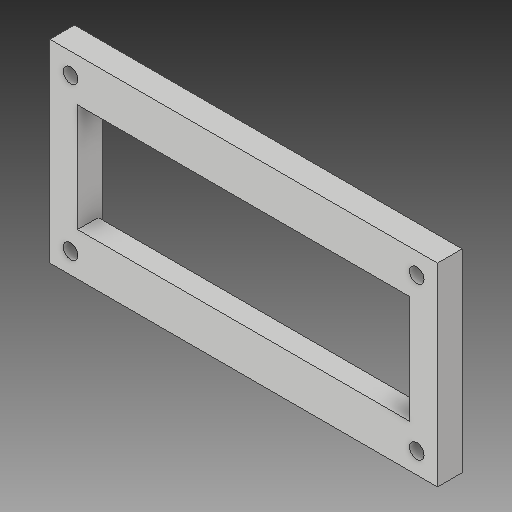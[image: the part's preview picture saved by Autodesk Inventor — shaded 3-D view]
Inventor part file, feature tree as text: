
AUTODESK INVENTOR PART (.ipt)
format: ipt  version: 2018 (Build 220112000, 112)  size: 131,584 bytes
history: native  units: in
note: dims shown in document units (in); Inventor stores cm internally (conversion verified against a paired STEP export)
features: sketch x3, extrude x2, hole x2, projected_geometry x1
ambient origin geometry x8: Origin, YZ Plane, XZ Plane, XY Plane, X Axis, Y Axis, Z Axis, Center Point
bodies: Body1 (feature_tree)
feature tree (8):
  extrude  "Extrusion6"  Depth=3.5in
  extrude  "Extrusion7"  Depth=6.0in
  hole  "Hole4"  [1 undecoded]
  sketch  "Sketch6"  dims[d36=7.0in d37=3.5in]
  sketch  "Sketch7"  dims[d38=2.2in d39=6.0in]
  projected_geometry  "Projected Loop4"
  sketch  "Sketch9"  dims[d40=0.07in d41=0.0in d42=0.125in d43=0.125in d44=0.375in d45=0.0in d53=0.266in d54=0.75in d55=0.375in d56=0.25in d57=0.5635in d58=1.0in d59=0.0in]
  hole  "Hole3"  [1 undecoded]
note: 2 required parameter values undecoded (feature->parameter linkage not recoverable at this tier; creation-order binding heuristic only, values carry confidence <= 0.55)
